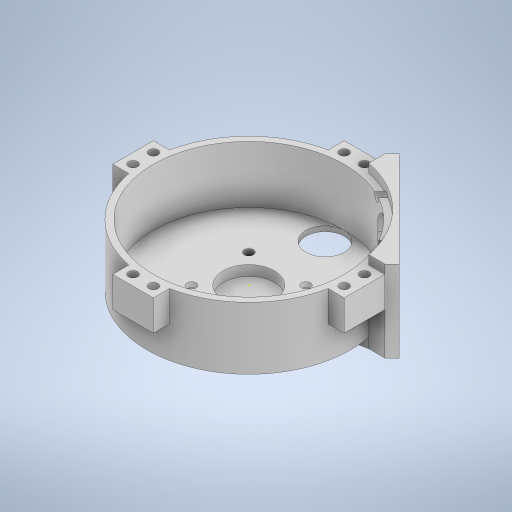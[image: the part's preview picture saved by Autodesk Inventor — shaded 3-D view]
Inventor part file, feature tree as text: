
AUTODESK INVENTOR PART (.ipt)
format: ipt  version: 2023 (Build 270158000, 158)  size: 526,336 bytes
history: native  units: in
note: dims shown in document units (in); Inventor stores cm internally (conversion verified against a paired STEP export)
features: sketch x19, extrude x15, hole x3
ambient origin geometry x8: Origin, YZ Plane, XZ Plane, XY Plane, X Axis, Y Axis, Z Axis, Center Point
bodies: Solid1 (feature_tree)
feature tree (37):
  extrude  "Extrusion1"  Depth=1.375in TaperAngle=0.0deg
  extrude  "Extrusion2"  Depth=1.275in TaperAngle=0.0deg
  extrude  "Extrusion3"  Depth=1.125in TaperAngle=0.0deg
  hole  "Hole1"  [1 undecoded]
  extrude  "Extrusion4"  Depth=0.4in
  extrude  "Extrusion5"  Depth=0.4in
  hole  "Hole2"  [1 undecoded]
  extrude  "Extrusion6"  Depth=0.4in
  sketch  "Sketch10"  dims[d26=0.8in d27=0.4in]
  extrude  "Extrusion7"  Depth=0.4in
  extrude  "Extrusion8"  Depth=0.8in
  extrude  "Extrusion9"  Depth=0.4in
  extrude  "Extrusion11"  Depth=0.75in TaperAngle=0.0deg
  extrude  "Extrusion12"  Depth=0.2in
  extrude  "Extrusion13"  Depth=0.2in
  extrude  "Extrusion14"  Depth=0.4in
  extrude  "Extrusion16"  Depth=0.2in
  hole  "Hole5"  [1 undecoded]
  extrude  "Extrusion17"  Depth=1.2in
  sketch  "Sketch1"  dims[d0=4.0in d1=1.375in d2=0.0in]
  sketch  "Sketch2"  dims[d3=3.75in d4=1.275in d5=0.0in]
  sketch  "Sketch3"  dims[d6=1.0in d7=1.125in d8=0.0in]
  sketch  "Sketch4"  dims[d9=1.125in d10=1.125in]
  sketch  "Sketch5"  dims[d11=0.177in d12=0.75in d13=0.332in d14=0.25in d15=0.5635in d16=1.0in d17=0.8108in d18=0.4in]
  sketch  "Sketch6"  dims[d19=0.4in d20=0.4in]
  sketch  "Sketch7"  dims[d21=0.4in d22=0.75in d23=0.0in]
  sketch  "Sketch8"  dims[d24=0.4in d25=0.4in]
  sketch  "Sketch11"  dims[d28=0.4in d29=0.8in]
  sketch  "Sketch12"  dims[d30=0.4in d31=0.4in]
  sketch  "Sketch13"  dims[d32=0.8in d33=0.75in d34=0.0in]
  sketch  "Sketch17"  dims[d35=0.2in d36=0.2in]
  sketch  "Sketch18"  dims[d37=0.4in d38=0.2in]
  sketch  "Sketch19"  dims[d39=0.2in d40=0.4in]
  sketch  "Sketch20"  dims[d41=0.2in d42=0.2in]
  sketch  "Sketch23"  dims[d43=0.2in d44=0.2in]
  sketch  "Sketch24"  dims[d45=0.4in]
  sketch  "Sketch25"  dims[d46=0.177in d47=0.75in d48=0.375in d49=0.25in d50=0.5635in d51=0.75in d52=0.8108in d53=1.5in d54=0.75in d55=0.0in d66=0.15in d67=0.0in d68=2.0in d69=0.275in d70=0.275in d71=0.275in d72=0.275in d73=0.1in d74=0.0in d75=0.1in d76=0.0in d79=0.175in d80=0.0in d81=0.2in d82=0.175in d83=0.0in d84=0.2in d85=0.0in d86=1.0875in d87=0.0in d101=1.425in d102=0.0in d103=1.425in d104=0.0in d105=0.3in d106=0.0in d107=0.8in d108=1.326in d109=1.18in d110=1.18in d111=0.169in d112=0.75in d113=0.375in d114=0.25in d115=0.5635in d116=0.75in d117=0.8108in d118=0.75in d119=1.2in d120=0.3in d121=0.0in]
note: 3 required parameter values undecoded (feature->parameter linkage not recoverable at this tier; creation-order binding heuristic only, values carry confidence <= 0.55)
